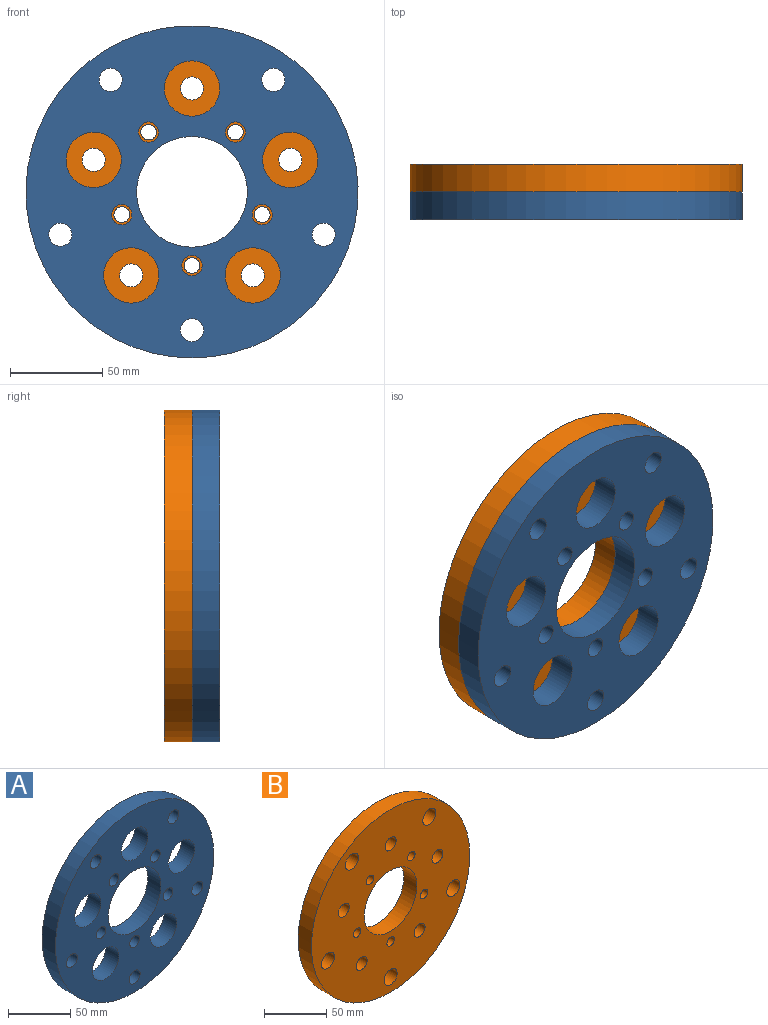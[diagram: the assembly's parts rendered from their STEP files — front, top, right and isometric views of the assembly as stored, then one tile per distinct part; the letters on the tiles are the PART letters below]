
ASSEMBLY  parts=2 mates=1
PART A: 19 faces, bbox 180x15x180 mm
  f0: cylinder r=90mm len=180mm, axis (0,1,0), area 8482.3mm2, adj f1,f2
  f1: plane 180x180mm, normal (0,-1,0), area 17996.4mm2, adj f0,f3,f4,f5,f6,f7,f8,f9
  f2: plane 180x180mm, normal (0,1,0), area 17996.4mm2, adj f0,f3,f4,f5,f6,f7,f8,f9
  f3: cylinder r=15mm len=30mm, axis (0,1,0), area 1413.7mm2, adj f1,f2
  f4: cylinder r=15mm len=30mm, axis (0,1,0), area 1413.7mm2, adj f1,f2
  f5: cylinder r=15mm len=30mm, axis (0,1,0), area 1413.7mm2, adj f1,f2
  f6: cylinder r=15mm len=30mm, axis (0,1,0), area 1413.7mm2, adj f1,f2
  f7: cylinder r=6.25mm len=15mm, axis (0,1,0), area 589mm2, adj f1,f2
  f8: cylinder r=6.25mm len=15mm, axis (0,1,0), area 589mm2, adj f1,f2
  f9: cylinder r=6.25mm len=15mm, axis (0,1,0), area 589mm2, adj f1,f2
  f10: cylinder r=6.25mm len=15mm, axis (0,1,0), area 589mm2, adj f1,f2
  f11: cylinder r=5.5mm len=15mm, axis (0,1,0), area 518.4mm2, adj f1,f2
  f12: cylinder r=5.5mm len=15mm, axis (0,1,0), area 518.4mm2, adj f1,f2
  f13: cylinder r=5.5mm len=15mm, axis (0,1,0), area 518.4mm2, adj f1,f2
  f14: cylinder r=15mm len=30mm, axis (0,1,0), area 1413.7mm2, adj f1,f2
  f15: cylinder r=30mm len=60mm, axis (0,1,0), area 2827.4mm2, adj f1,f2
  f16: cylinder r=5.5mm len=15mm, axis (0,1,0), area 518.4mm2, adj f1,f2
  f17: cylinder r=5.5mm len=15mm, axis (0,1,0), area 518.4mm2, adj f1,f2
  f18: cylinder r=6.25mm len=15mm, axis (0,1,0), area 589mm2, adj f1,f2
PART B: 19 faces, bbox 180x15x180 mm
  f0: cylinder r=90mm len=180mm, axis (0,1,0), area 8482.3mm2, adj f1,f2
  f1: plane 180x180mm, normal (0,-1,0), area 20838.6mm2, adj f0,f3,f4,f5,f6,f7,f8,f9
  f2: plane 180x180mm, normal (0,1,0), area 20838.6mm2, adj f0,f3,f4,f5,f6,f7,f8,f9
  f3: cylinder r=6.25mm len=15mm, axis (0,1,0), area 589mm2, adj f1,f2
  f4: cylinder r=6.25mm len=15mm, axis (0,1,0), area 589mm2, adj f1,f2
  f5: cylinder r=6.25mm len=15mm, axis (0,1,0), area 589mm2, adj f1,f2
  f6: cylinder r=6.25mm len=15mm, axis (0,1,0), area 589mm2, adj f1,f2
  f7: cylinder r=7.5mm len=15mm, axis (0,1,0), area 706.9mm2, adj f1,f2
  f8: cylinder r=7.5mm len=15mm, axis (0,1,0), area 706.9mm2, adj f1,f2
  f9: cylinder r=7.5mm len=15mm, axis (0,1,0), area 706.9mm2, adj f1,f2
  f10: cylinder r=7.5mm len=15mm, axis (0,1,0), area 706.9mm2, adj f1,f2
  f11: cylinder r=4.25mm len=15mm, axis (0,1,0), area 400.6mm2, adj f1,f2
  f12: cylinder r=4.25mm len=15mm, axis (0,1,0), area 400.6mm2, adj f1,f2
  f13: cylinder r=4.25mm len=15mm, axis (0,1,0), area 400.6mm2, adj f1,f2
  f14: cylinder r=6.25mm len=15mm, axis (0,1,0), area 589mm2, adj f1,f2
  f15: cylinder r=30mm len=60mm, axis (0,1,0), area 2827.4mm2, adj f1,f2
  f16: cylinder r=4.25mm len=15mm, axis (0,1,0), area 400.6mm2, adj f1,f2
  f17: cylinder r=4.25mm len=15mm, axis (0,1,0), area 400.6mm2, adj f1,f2
  f18: cylinder r=7.5mm len=15mm, axis (0,1,0), area 706.9mm2, adj f1,f2
PLACE A t=(-61.51,-45.12,-3.16)mm
PLACE B t=(-61.51,-30.12,-3.16)mm
MATE planar A.f0 <-> B.f0  axis (0,1,0) through (-61.51,-45.12,-3.16)mm
